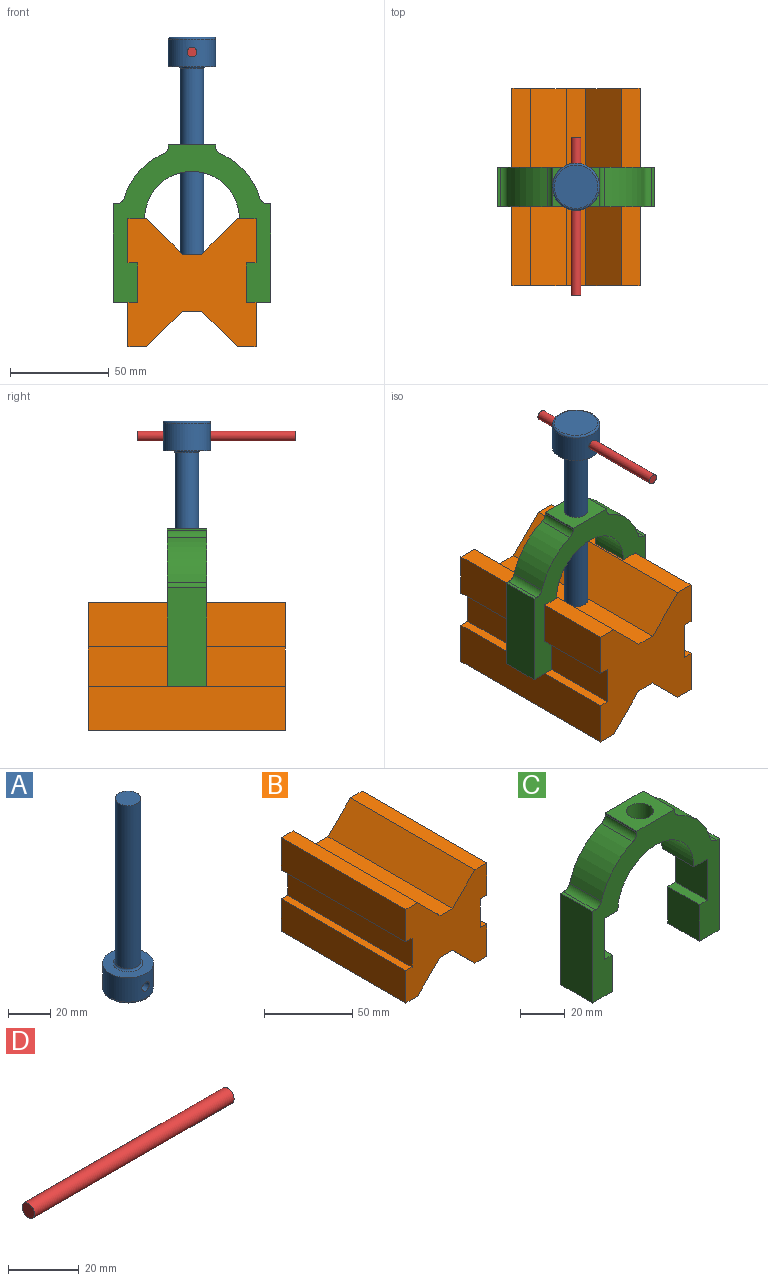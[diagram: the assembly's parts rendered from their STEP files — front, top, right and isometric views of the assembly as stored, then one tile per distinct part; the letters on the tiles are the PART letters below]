
ASSEMBLY  parts=4 mates=3
PART A: 8 faces, bbox 26x26x110 mm
  f0: cylinder r=12mm len=24mm, axis (0,0,-1), area 1015.9mm2, adj f1,f6,f7
  f1: plane 24x24mm, normal (0,0,1), area 298.5mm2, adj f0,f5
  f2: plane 22x22mm, normal (0,0,-1), area 380.1mm2, adj f6
  f3: cylinder r=6mm len=94mm, axis (0,0,-1), area 3543.7mm2, adj f4,f5
  f4: plane 12x12mm, normal (0,0,1), area 113.1mm2, adj f3
  f5: torus R=7mm, axis (0,0,1), area 62.8mm2, adj f1,f3
  f6: torus R=11mm, axis (0,0,1), area 114.8mm2, adj f0,f2
  f7: cylinder r=2.5mm len=24mm, axis (0,-1,0), area 372.9mm2, adj f0
PART B: 22 faces, bbox 65x100x65 mm
  f0: plane 100x10mm, normal (0,0,-1), area 1000mm2, adj f1,f19,f20,f21
  f1: plane 100x18mm, normal (-0.71,0,-0.71), area 2545.6mm2, adj f0,f2,f20,f21
  f2: plane 100x9.5mm, normal (0,0,-1), area 950mm2, adj f1,f3,f20,f21
  f3: plane 100x22.5mm, normal (1,0,0), area 2250mm2, adj f2,f4,f20,f21
  f4: plane 100x5mm, normal (0,0,1), area 500mm2, adj f3,f5,f20,f21
  f5: plane 100x20mm, normal (1,0,0), area 2000mm2, adj f4,f6,f20,f21
  f6: plane 100x5mm, normal (0,0,-1), area 500mm2, adj f5,f7,f20,f21
  f7: plane 100x22.5mm, normal (1,0,0), area 2250mm2, adj f6,f8,f20,f21
  f8: plane 100x9.5mm, normal (0,0,1), area 950mm2, adj f7,f9,f20,f21
  f9: plane 100x18mm, normal (-0.71,0,0.71), area 2545.6mm2, adj f8,f10,f20,f21
  f10: plane 100x10mm, normal (0,0,1), area 1000mm2, adj f9,f11,f20,f21
  f11: plane 100x18mm, normal (0.71,0,0.71), area 2545.6mm2, adj f10,f12,f20,f21
  f12: plane 100x9.5mm, normal (0,0,1), area 950mm2, adj f11,f13,f20,f21
  f13: plane 100x22.5mm, normal (-1,0,0), area 2250mm2, adj f12,f14,f20,f21
  f14: plane 100x5mm, normal (0,0,-1), area 500mm2, adj f13,f15,f20,f21
  f15: plane 100x20mm, normal (-1,0,0), area 2000mm2, adj f14,f16,f20,f21
  f16: plane 100x5mm, normal (0,0,1), area 500mm2, adj f15,f17,f20,f21
  f17: plane 100x22.5mm, normal (-1,0,0), area 2250mm2, adj f16,f18,f20,f21
  f18: plane 100x9.5mm, normal (0,0,-1), area 950mm2, adj f17,f19,f20,f21
  f19: plane 100x18mm, normal (0.71,0,-0.71), area 2545.6mm2, adj f0,f18,f20,f21
  f20: plane 65x65mm, normal (0,-1,0), area 3017mm2, adj f0,f1,f2,f3,f4,f5,f6,f7
  f21: plane 65x65mm, normal (0,1,0), area 3017mm2, adj f0,f1,f2,f3,f4,f5,f6,f7
PART C: 27 faces, bbox 80x20x80 mm
  f0: cylinder r=24mm len=48mm, axis (0,1,0), area 1393.8mm2, adj f1,f23,f24,f25,f26
  f1: plane 20x8.5mm, normal (0,0,-1), area 170mm2, adj f0,f2,f24,f25
  f2: plane 22.5x20mm, normal (-1,0,0), area 450mm2, adj f1,f3,f24,f25
  f3: plane 20x5mm, normal (0,0,1), area 100mm2, adj f2,f4,f24,f25
  f4: plane 20x20mm, normal (-1,0,0), area 400mm2, adj f3,f5,f24,f25
  f5: plane 20x12.5mm, normal (0,0,-1), area 250mm2, adj f4,f6,f24,f25
  f6: plane 50x20mm, normal (1,0,0), area 1000mm2, adj f5,f7,f24,f25
  f7: plane 20x1.69mm, normal (0,0,1), area 33.8mm2, adj f6,f8,f24,f25
  f8: cylinder r=4mm len=20mm, axis (0,1,0), area 102.3mm2, adj f7,f9,f24,f25
  f9: cylinder r=36mm len=22.64mm, axis (0,1,0), area 624.7mm2, adj f8,f10,f24,f25
  f10: cylinder r=4mm len=20mm, axis (0,1,0), area 92.7mm2, adj f9,f11,f24,f25
  f11: plane 20x0.84mm, normal (1,0,0), area 16.8mm2, adj f10,f12,f24,f25
  f12: plane 24x20mm, normal (0,0,1), area 366.9mm2, adj f11,f13,f24,f25,f26
  f13: plane 20x0.84mm, normal (-1,0,0), area 16.8mm2, adj f12,f14,f24,f25
  f14: cylinder r=4mm len=20mm, axis (0,1,0), area 92.7mm2, adj f13,f15,f24,f25
  f15: cylinder r=36mm len=22.64mm, axis (0,1,0), area 624.7mm2, adj f14,f16,f24,f25
  f16: cylinder r=4mm len=20mm, axis (0,1,0), area 102.3mm2, adj f15,f17,f24,f25
  f17: plane 20x1.69mm, normal (0,0,1), area 33.8mm2, adj f16,f18,f24,f25
  f18: plane 50x20mm, normal (-1,0,0), area 1000mm2, adj f17,f19,f24,f25
  f19: plane 20x12.5mm, normal (0,0,-1), area 250mm2, adj f18,f20,f24,f25
  f20: plane 20x20mm, normal (1,0,0), area 400mm2, adj f19,f21,f24,f25
  f21: plane 20x5mm, normal (0,0,1), area 100mm2, adj f20,f22,f24,f25
  f22: plane 22.5x20mm, normal (1,0,0), area 450mm2, adj f21,f23,f24,f25
  f23: plane 20x8.5mm, normal (0,0,-1), area 170mm2, adj f0,f22,f24,f25
  f24: plane 80x80mm, normal (0,-1,0), area 2090.8mm2, adj f0,f1,f2,f3,f4,f5,f6,f7
  f25: plane 80x80mm, normal (0,1,0), area 2090.8mm2, adj f0,f1,f2,f3,f4,f5,f6,f7
  f26: cylinder r=6mm len=14.26mm, axis (0,0,-1), area 523.3mm2, adj f0,f12
PART D: 3 faces, bbox 80x5x5 mm
  f0: cylinder r=2.5mm len=80mm, axis (-1,0,0), area 1256.6mm2, adj f1,f2
  f1: plane 5x5mm, normal (1,0,0), area 19.6mm2, adj f0
  f2: plane 5x5mm, normal (-1,0,0), area 19.6mm2, adj f0
PLACE A rot(axis=(1,0,0),180deg) t=(38.22,-20.83,226.84)mm
PLACE B t=(38.22,29.17,102.34)mm
PLACE C t=(38.22,-20.83,134.84)mm
PLACE D rot(axis=(-0.58,0.58,-0.58),120deg) t=(38.22,4,219.34)mm
MATE slider A.f7 <-> D.f0  axis (0,1,0) through (38.22,-20.83,219.34)mm
MATE fastened A.f0 <-> B.f10  axis (0,0,-1) through (38.22,-20.83,116.84)mm
MATE fastened B.f13 <-> C.f22  axis (-1,0,0) through (5.72,-20.83,123.59)mm
